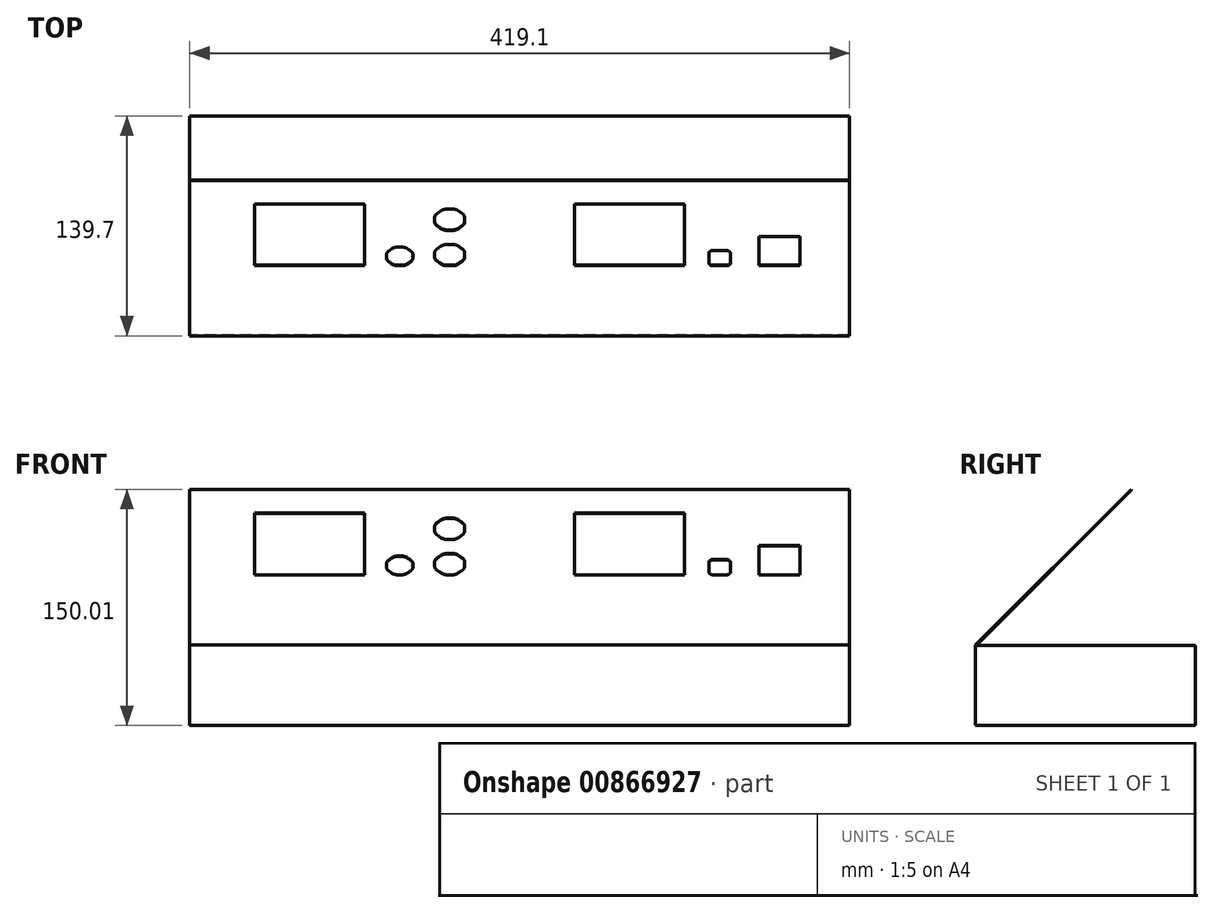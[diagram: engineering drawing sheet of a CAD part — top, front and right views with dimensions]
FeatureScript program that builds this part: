
annotation { "Feature Type Name" : "Feature", "Feature Type Description" : "" }
export const myFeature = defineFeature(function(context is Context, id is Id, definition is map)
    precondition{}
    {
        {
            var Q0;
            Q0=qCreatedBy(makeId("Right.planeOp"),FACE);
            var sketch = newSketch(context, id + "F0", { "sketchPlane" : qUnion([Q0])});
            skLineSegment(sketch, "E0.bottom", {"start": v(0, 0) * mm, "end": v(-139.7, 0) * mm});
            skLineSegment(sketch, "E0.top", {"start": v(0, 50.8) * mm, "end": v(-139.3, 50.8) * mm});
            skLineSegment(sketch, "E0.left", {"start": v(0, 0) * mm, "end": v(0, 50.8) * mm});
            skLineSegment(sketch, "E0.right", {"start": v(-139.7, 0) * mm, "end": v(-139.7, 51.22) * mm});
            skLineSegment(sketch, "E1", {"start": v(-139.7, 51.22) * mm, "end": v(-40.92, 150) * mm});
            skLineSegment(sketch, "E2", {"start": v(-40.92, 150) * mm, "end": v(-40.63, 149.72) * mm});
            skLineSegment(sketch, "E3", {"start": v(-40.63, 149.72) * mm, "end": v(-139.3, 51.05) * mm});
            skLineSegment(sketch, "E4", {"start": v(-139.3, 50.8) * mm, "end": v(-139.3, 51.05) * mm});
            skLineSegment(sketch, "E5", {"start": v(-139.3, 50.8) * mm, "end": v(-139.7, 50.8) * mm, "construction": true});
            skSolve(sketch);
        }
        {
            var Q0;
            Q0=qSketchRegion(id+"F0",true);
            extrude(context, id + "F1", {"entities" : qUnion([Q0]), "endBound" : BoundingType.SYMMETRIC, "depth" : 419.1 * mm, "offsetDistance" : 25.4 * mm});
        }
        {
            var Q0;
            Q0=makeQuery(id+"F1.opExtrude","SWEPT_FACE",FACE,{"disambiguationData":[OSD([sQuery(id+"F0.wireOp",EDGE,"E1")])]});
            var sketch = newSketch(context, id + "F2", { "sketchPlane" : qUnion([Q0])});
            skLineSegment(sketch, "E6", {"start": v(-98.49, 0.51) * mm, "end": v(-98.49, 56.08) * mm});
            skLineSegment(sketch, "E7", {"start": v(-98.49, 56.08) * mm, "end": v(-168.34, 56.08) * mm});
            skLineSegment(sketch, "E8", {"start": v(-168.34, 56.08) * mm, "end": v(-168.34, 0.51) * mm});
            skLineSegment(sketch, "E9", {"start": v(-168.34, 0.51) * mm, "end": v(-98.49, 0.51) * mm});
            skLineSegment(sketch, "E10", {"start": v(34.86, 0.51) * mm, "end": v(104.71, 0.51) * mm});
            skLineSegment(sketch, "E11", {"start": v(34.86, 56.08) * mm, "end": v(34.86, 0.51) * mm});
            skLineSegment(sketch, "E12", {"start": v(104.71, 56.08) * mm, "end": v(34.86, 56.08) * mm});
            skLineSegment(sketch, "E13", {"start": v(104.71, 0.51) * mm, "end": v(104.71, 56.08) * mm});
            skLineSegment(sketch, "E14", {"start": v(120.2, 11.63) * mm, "end": v(120.2, 2.9) * mm});
            skLineSegment(sketch, "E15", {"start": v(133.69, 2.9) * mm, "end": v(133.69, 11.63) * mm});
            skLineSegment(sketch, "E16", {"start": v(151.94, 0.51) * mm, "end": v(178.14, 0.51) * mm});
            skLineSegment(sketch, "E17", {"start": v(151.94, 26.7) * mm, "end": v(151.94, 0.51) * mm});
            skLineSegment(sketch, "E18", {"start": v(178.14, 26.7) * mm, "end": v(151.94, 26.7) * mm});
            skLineSegment(sketch, "E19", {"start": v(178.14, 0.51) * mm, "end": v(178.14, 26.7) * mm});
            skLineSegment(sketch, "E20", {"start": v(-209.61, -62.99) * mm, "end": v(-209.61, 75.92) * mm, "construction": true});
            skLineSegment(sketch, "E21", {"start": v(209.49, -62.99) * mm, "end": v(209.49, 75.92) * mm, "construction": true});
            skLineSegment(sketch, "E22", {"start": v(-209.61, 75.92) * mm, "end": v(209.49, 75.92) * mm, "construction": true});
            skLineSegment(sketch, "E23", {"start": v(131.3, 14) * mm, "end": v(122.57, 14) * mm});
            skLineSegment(sketch, "E24", {"start": v(122.57, 0.51) * mm, "end": v(131.3, 0.51) * mm});
            skLineSegment(sketch, "E25", {"start": v(209.49, -62.99) * mm, "end": v(-209.61, -62.99) * mm, "construction": true});
            skFitSpline(sketch, "E26", {"points": [v(-76.26, 17.18) * mm, v(-78.44, 17.18) * mm, v(-80.61, 16.28) * mm, v(-82.15, 14.74) * mm]});
            skFitSpline(sketch, "E27", {"points": [v(-82.15, 14.74) * mm, v(-83.7, 13.2) * mm, v(-84.6, 11.03) * mm, v(-84.6, 8.85) * mm, v(-84.6, 6.67) * mm, v(-83.7, 4.5) * mm, v(-82.15, 2.95) * mm]});
            skFitSpline(sketch, "E28", {"points": [v(-82.15, 2.95) * mm, v(-80.61, 1.41) * mm, v(-78.44, 0.51) * mm, v(-76.26, 0.51) * mm, v(-74.08, 0.51) * mm, v(-71.91, 1.41) * mm, v(-70.37, 2.95) * mm]});
            skFitSpline(sketch, "E29", {"points": [v(-70.37, 2.95) * mm, v(-68.83, 4.5) * mm, v(-67.93, 6.67) * mm, v(-67.93, 8.85) * mm, v(-67.93, 11.03) * mm, v(-68.83, 13.2) * mm, v(-70.37, 14.74) * mm]});
            skFitSpline(sketch, "E30", {"points": [v(-70.37, 14.74) * mm, v(-71.91, 16.28) * mm, v(-74.08, 17.18) * mm, v(-76.26, 17.18) * mm]});
            skFitSpline(sketch, "E31", {"points": [v(-44.51, 19.56) * mm, v(-47, 19.56) * mm, v(-49.48, 18.54) * mm, v(-51.25, 16.77) * mm]});
            skFitSpline(sketch, "E32", {"points": [v(-51.25, 16.77) * mm, v(-53, 15) * mm, v(-54.04, 12.53) * mm, v(-54.04, 10.04) * mm, v(-54.04, 7.54) * mm, v(-53, 5.07) * mm, v(-51.25, 3.3) * mm]});
            skFitSpline(sketch, "E33", {"points": [v(-51.25, 3.3) * mm, v(-49.48, 1.54) * mm, v(-47, 0.51) * mm, v(-44.51, 0.51) * mm, v(-42.02, 0.51) * mm, v(-39.54, 1.54) * mm, v(-37.78, 3.3) * mm]});
            skFitSpline(sketch, "E34", {"points": [v(-37.78, 3.3) * mm, v(-36.01, 5.07) * mm, v(-34.99, 7.54) * mm, v(-34.99, 10.04) * mm, v(-34.99, 12.53) * mm, v(-36.01, 15) * mm, v(-37.78, 16.77) * mm]});
            skFitSpline(sketch, "E35", {"points": [v(-37.78, 16.77) * mm, v(-39.54, 18.54) * mm, v(-42.02, 19.56) * mm, v(-44.51, 19.56) * mm]});
            skFitSpline(sketch, "E36", {"points": [v(-44.51, 51.31) * mm, v(-47, 51.31) * mm, v(-49.48, 50.29) * mm, v(-51.25, 48.52) * mm]});
            skFitSpline(sketch, "E37", {"points": [v(-51.25, 48.52) * mm, v(-53, 46.76) * mm, v(-54.04, 44.28) * mm, v(-54.04, 41.79) * mm, v(-54.04, 39.3) * mm, v(-53, 36.82) * mm, v(-51.25, 35.05) * mm]});
            skFitSpline(sketch, "E38", {"points": [v(-51.25, 35.05) * mm, v(-49.48, 33.29) * mm, v(-47, 32.26) * mm, v(-44.51, 32.26) * mm, v(-42.02, 32.26) * mm, v(-39.54, 33.29) * mm, v(-37.78, 35.05) * mm]});
            skFitSpline(sketch, "E39", {"points": [v(-37.78, 35.05) * mm, v(-36.01, 36.82) * mm, v(-34.99, 39.3) * mm, v(-34.99, 41.79) * mm, v(-34.99, 44.28) * mm, v(-36.01, 46.76) * mm, v(-37.78, 48.52) * mm]});
            skFitSpline(sketch, "E40", {"points": [v(-37.78, 48.52) * mm, v(-39.54, 50.29) * mm, v(-42.02, 51.31) * mm, v(-44.51, 51.31) * mm]});
            skFitSpline(sketch, "E41", {"points": [v(120.2, 2.9) * mm, v(120.2, 2.27) * mm, v(120.45, 1.65) * mm, v(120.89, 1.21) * mm]});
            skFitSpline(sketch, "E42", {"points": [v(120.89, 1.21) * mm, v(121.33, 0.77) * mm, v(121.95, 0.51) * mm, v(122.57, 0.51) * mm]});
            skFitSpline(sketch, "E43", {"points": [v(122.57, 14) * mm, v(121.95, 14) * mm, v(121.33, 13.75) * mm, v(120.89, 13.3) * mm]});
            skFitSpline(sketch, "E44", {"points": [v(120.89, 13.3) * mm, v(120.45, 12.87) * mm, v(120.2, 12.25) * mm, v(120.2, 11.63) * mm]});
            skFitSpline(sketch, "E45", {"points": [v(133.69, 11.63) * mm, v(133.69, 12.25) * mm, v(133.43, 12.87) * mm, v(132.99, 13.3) * mm]});
            skFitSpline(sketch, "E46", {"points": [v(132.99, 13.3) * mm, v(132.55, 13.75) * mm, v(131.93, 14) * mm, v(131.3, 14) * mm]});
            skFitSpline(sketch, "E47", {"points": [v(131.3, 0.51) * mm, v(131.93, 0.51) * mm, v(132.55, 0.77) * mm, v(132.99, 1.21) * mm]});
            skFitSpline(sketch, "E48", {"points": [v(132.99, 1.21) * mm, v(133.43, 1.65) * mm, v(133.69, 2.27) * mm, v(133.69, 2.9) * mm]});
            skSolve(sketch);
        }
        {
            var Q0;
            Q0=qSketchRegion(id+"F2",true);
            var Q1;
            Q1=makeQuery(id+"F1.opExtrude","SWEPT_FACE",FACE,{"disambiguationData":[OSD([sQuery(id+"F0.wireOp",EDGE,"E3")])]});
            extrude(context, id + "F3", {"entities" : qUnion([Q0]), "operationType" : NewBodyOperationType.REMOVE, "endBound" : BoundingType.UP_TO_SURFACE, "oppositeDirection" : true, "depth" : 25.4 * mm, "endBoundEntityFace" : qUnion([Q1]), "offsetDistance" : 25.4 * mm});
        }
    });
